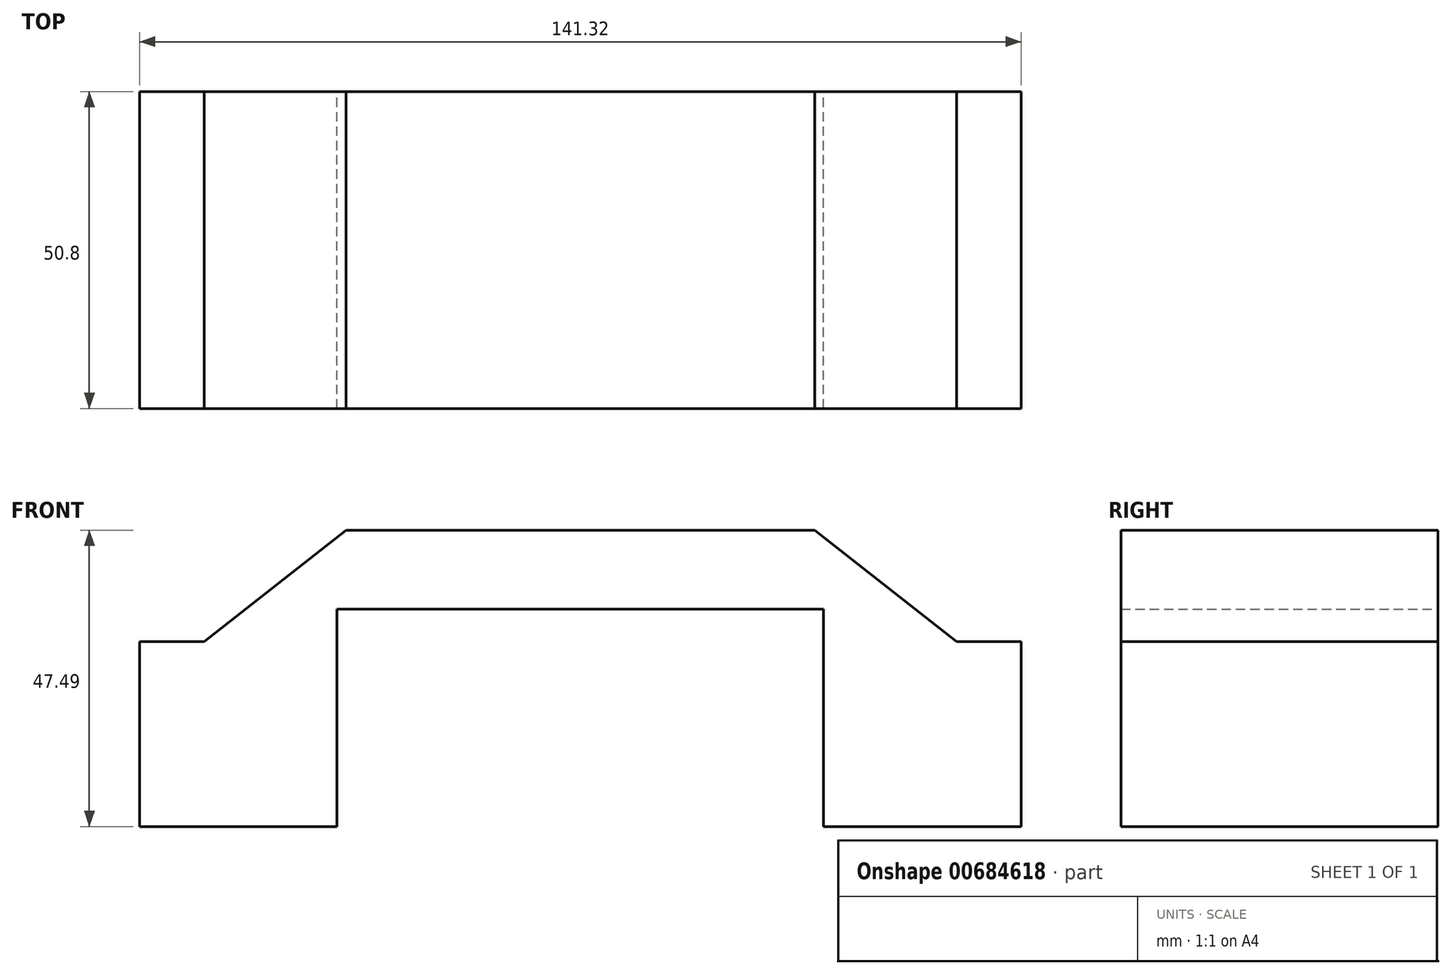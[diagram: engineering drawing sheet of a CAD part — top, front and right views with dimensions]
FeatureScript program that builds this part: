
annotation { "Feature Type Name" : "Feature", "Feature Type Description" : "" }
export const myFeature = defineFeature(function(context is Context, id is Id, definition is map)
    precondition{}
    {
        {
            var Q0;
            Q0=qCreatedBy(makeId("Front.planeOp"),FACE);
            var sketch = newSketch(context, id + "F0", { "sketchPlane" : qUnion([Q0])});
            skLineSegment(sketch, "E0", {"start": v(0, 33.53) * mm, "end": v(37.56, 33.53) * mm});
            skLineSegment(sketch, "E1", {"start": v(37.56, 33.53) * mm, "end": v(60.3, 15.69) * mm});
            skLineSegment(sketch, "E2", {"start": v(60.3, 15.69) * mm, "end": v(70.66, 15.69) * mm});
            skLineSegment(sketch, "E3", {"start": v(70.66, 15.69) * mm, "end": v(70.66, -13.96) * mm});
            skLineSegment(sketch, "E4", {"start": v(70.66, -13.96) * mm, "end": v(39, -13.96) * mm});
            skLineSegment(sketch, "E5", {"start": v(39, -13.96) * mm, "end": v(39, 20.87) * mm});
            skLineSegment(sketch, "E6", {"start": v(39, 20.87) * mm, "end": v(0, 20.87) * mm});
            skLineSegment(sketch, "E7", {"start": v(0, 20.87) * mm, "end": v(0, 33.53) * mm});
            skLineSegment(sketch, "E8.MirrorCS", {"start": v(-70.66, 15.69) * mm, "end": v(-70.66, -13.96) * mm});
            skLineSegment(sketch, "E9.MirrorCS", {"start": v(-70.66, -13.96) * mm, "end": v(-39, -13.96) * mm});
            skLineSegment(sketch, "E10.MirrorCS", {"start": v(-60.3, 15.69) * mm, "end": v(-70.66, 15.69) * mm});
            skLineSegment(sketch, "E11.MirrorCS", {"start": v(-37.56, 33.53) * mm, "end": v(-60.3, 15.69) * mm});
            skLineSegment(sketch, "E12.MirrorCS", {"start": v(0, 33.53) * mm, "end": v(-37.56, 33.53) * mm});
            skLineSegment(sketch, "E13.MirrorCS", {"start": v(-39, -13.96) * mm, "end": v(-39, 20.87) * mm});
            skLineSegment(sketch, "E14.MirrorCS", {"start": v(-39, 20.87) * mm, "end": v(0, 20.87) * mm});
            skSolve(sketch);
        }
        {
            var Q0;
            Q0 = qSketchRegion(id + "F0", true);
            extrude(context, id + "F1", {"entities" : qUnion([Q0]), "depth" : 25.4 * mm, "offsetDistance" : 25.4 * mm, "hasSecondDirection" : true, "secondDirectionOppositeDirection" : true, "secondDirectionDepth" : 25.4 * mm});
        }
    });
